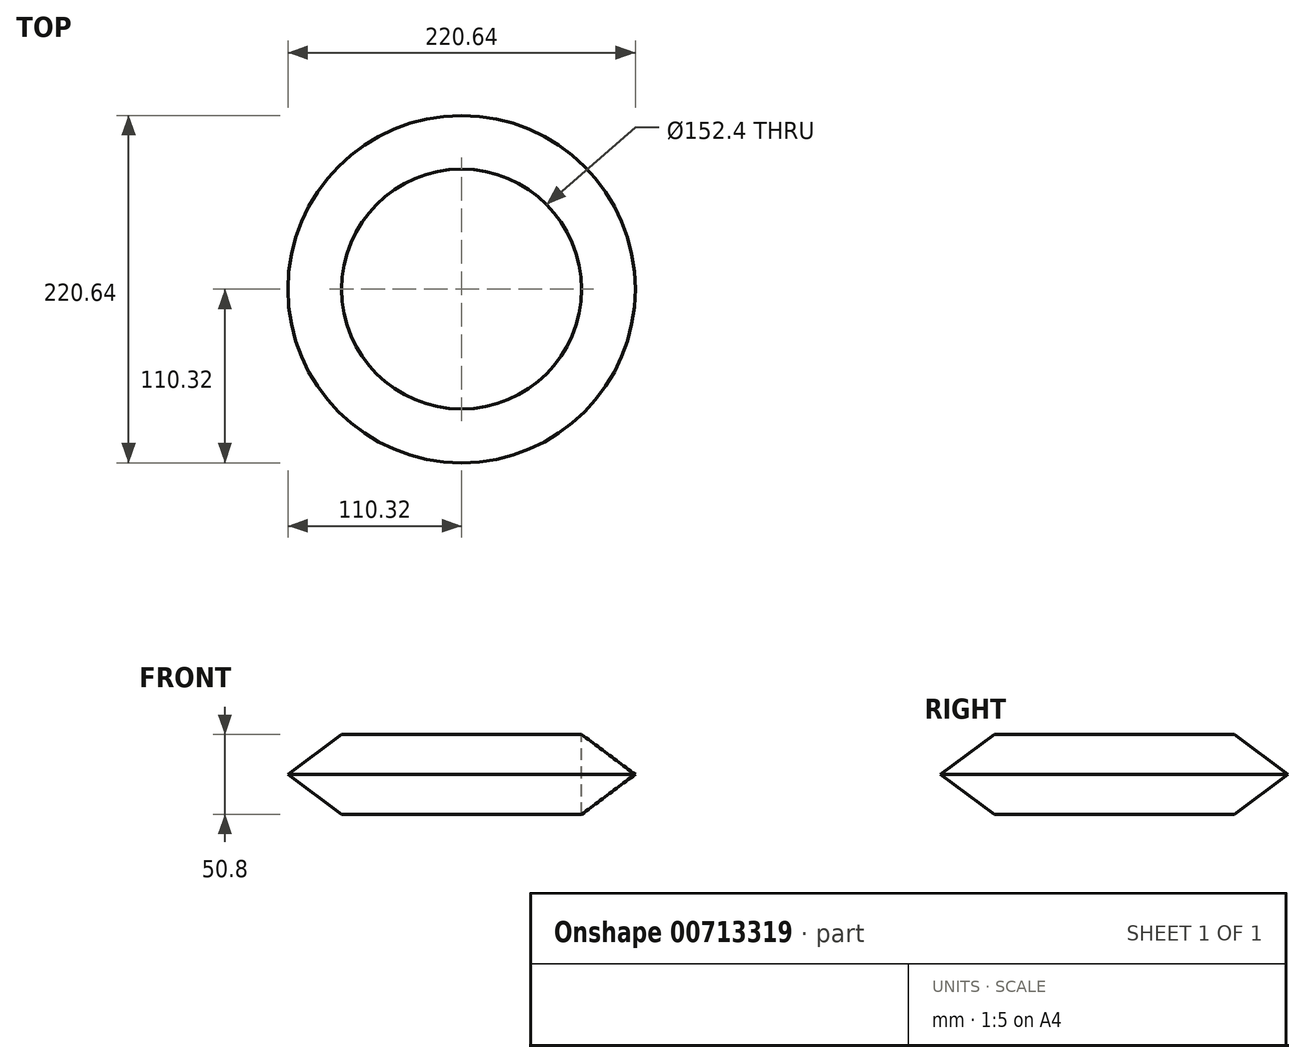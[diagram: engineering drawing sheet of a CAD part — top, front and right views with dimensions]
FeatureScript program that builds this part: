
annotation { "Feature Type Name" : "Feature", "Feature Type Description" : "" }
export const myFeature = defineFeature(function(context is Context, id is Id, definition is map)
    precondition{}
    {
        {
            var Q0;
            Q0=qCreatedBy(makeId("Front.planeOp"),FACE);
            var sketch = newSketch(context, id + "F0", { "sketchPlane" : qUnion([Q0])});
            skLineSegment(sketch, "E0", {"start": v(110.32, 0) * mm, "end": v(0, 0) * mm});
            skLineSegment(sketch, "E1", {"start": v(0, 0) * mm, "end": v(110.32, 0) * mm});
            skLineSegment(sketch, "E2", {"start": v(76.2, 25.4) * mm, "end": v(110.32, 0) * mm});
            skLineSegment(sketch, "E3", {"start": v(76.2, -25.4) * mm, "end": v(76.2, 25.4) * mm});
            skLineSegment(sketch, "E4", {"start": v(76.2, -25.4) * mm, "end": v(110.32, 0) * mm});
            skLineSegment(sketch, "E5", {"start": v(0, 22.6) * mm, "end": v(0, 0) * mm});
            skSolve(sketch);
        }
        {
            var Q0;
            {var subQ0=sQuery(id+"F0.wireOp",EDGE,"E2");Q0=makeQuery(id+"F0.imprint","IMPRINT",FACE,{"disambiguationData":[TD([[makeQuery(id+"F0.imprint","IMPRINT",EDGE,{"derivedFrom":subQ0}),-1.0]])]});}
            var Q1;
            {var subQ0=sQuery(id+"F0.wireOp",EDGE,"E4");Q1=makeQuery(id+"F0.imprint","IMPRINT",FACE,{"disambiguationData":[TD([[makeQuery(id+"F0.imprint","IMPRINT",EDGE,{"derivedFrom":subQ0}),1.0]])]});}
            var Q2;
            Q2=sQuery(id+"F0.wireOp",EDGE,"E5");
            revolve(context, id + "F1", {"surfaceOperationType" : NewSurfaceOperationType.NEW, "entities" : qUnion([Q0, Q1]), "axis" : qUnion([Q2]), "revolveType" : RevolveType.FULL});
        }
    });
